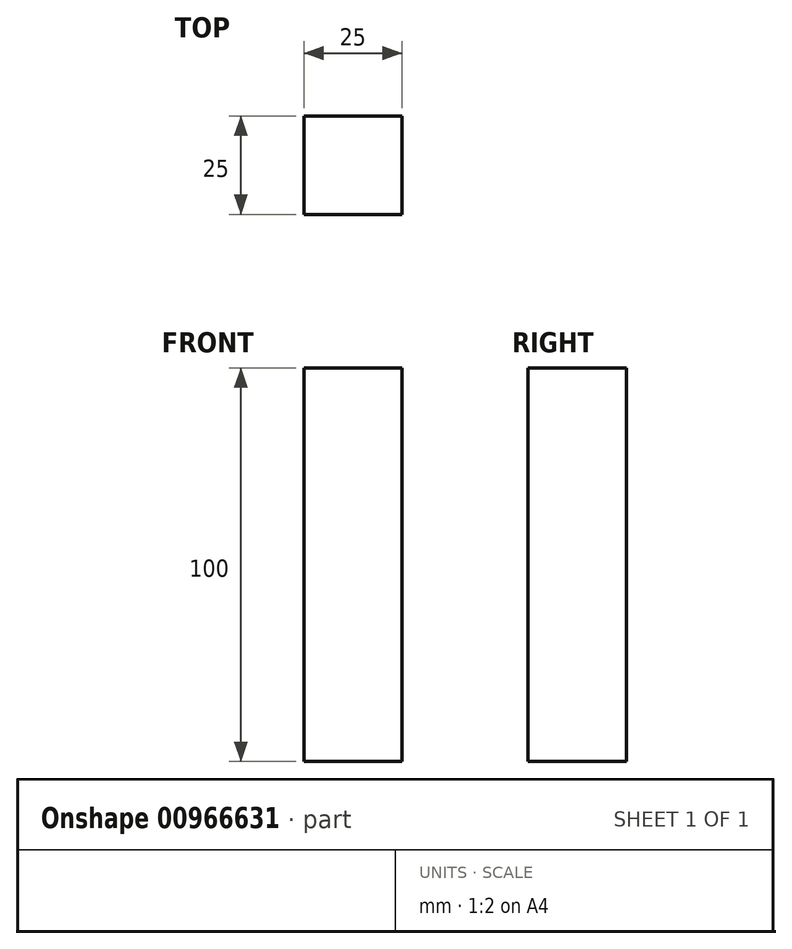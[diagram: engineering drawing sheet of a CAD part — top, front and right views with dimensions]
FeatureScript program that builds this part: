
annotation { "Feature Type Name" : "Feature", "Feature Type Description" : "" }
export const myFeature = defineFeature(function(context is Context, id is Id, definition is map)
    precondition{}
    {
        {
            var Q0;
            Q0=qCreatedBy(makeId("Top.planeOp"),FACE);
            var sketch = newSketch(context, id + "F0", { "sketchPlane" : qUnion([Q0])});
            skLineSegment(sketch, "E0.bottom", {"start": v(-7.43, 3.49) * mm, "end": v(17.57, 3.49) * mm});
            skLineSegment(sketch, "E0.top", {"start": v(-7.43, -21.51) * mm, "end": v(17.57, -21.51) * mm});
            skLineSegment(sketch, "E0.left", {"start": v(-7.43, 3.49) * mm, "end": v(-7.43, -21.51) * mm});
            skLineSegment(sketch, "E0.right", {"start": v(17.57, 3.49) * mm, "end": v(17.57, -21.51) * mm});
            skSolve(sketch);
        }
        {
            var Q0;
            Q0=makeQuery(id+"F0.imprint","IMPRINT",FACE,{"disambiguationData":[TD([[makeQuery(id+"F0.imprint","IMPRINT",EDGE,{"derivedFrom":sQuery(id+"F0.wireOp",EDGE,"E0.bottom")}),-1.0]])]});
            extrude(context, id + "F1", {"entities" : qUnion([Q0]), "depth" : 100 * mm, "offsetDistance" : 25 * mm});
        }
    });
